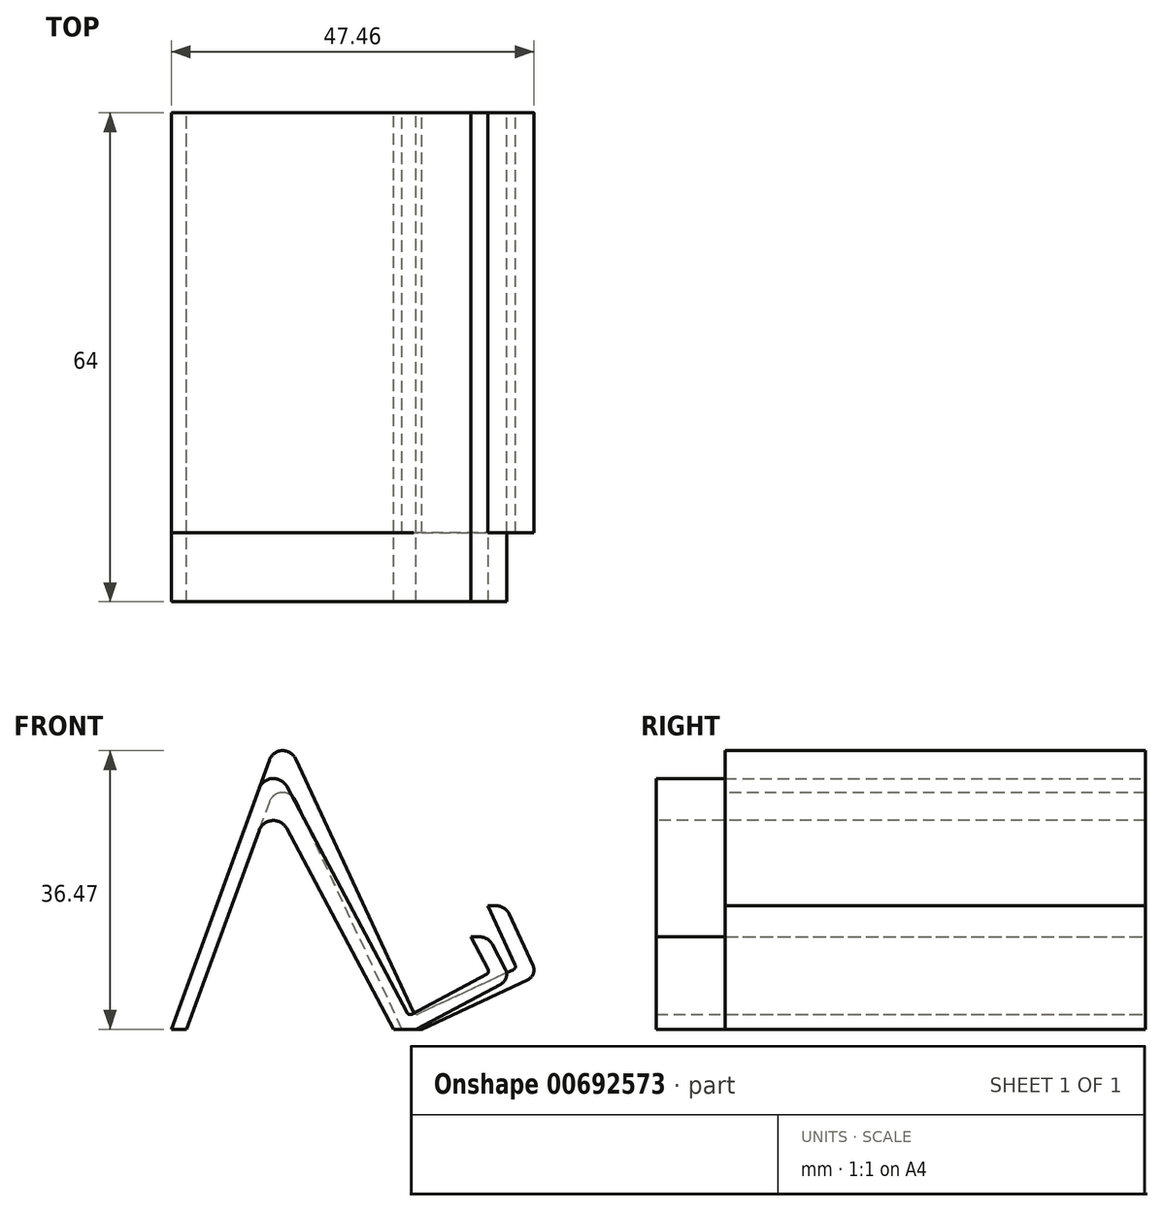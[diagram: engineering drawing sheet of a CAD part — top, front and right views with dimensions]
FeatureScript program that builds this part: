
annotation { "Feature Type Name" : "Feature", "Feature Type Description" : "" }
export const myFeature = defineFeature(function(context is Context, id is Id, definition is map)
    precondition{}
    {
        {
            var Q0;
            Q0=qCreatedBy(makeId("Front.planeOp"),FACE);
            var sketch = newSketch(context, id + "F0", { "sketchPlane" : qUnion([Q0])});
            skLineSegment(sketch, "E0", {"start": v(16.06, 0) * mm, "end": v(0, 30.21) * mm});
            skLineSegment(sketch, "E1", {"start": v(0, 30.21) * mm, "end": v(-11, 0) * mm});
            skLineSegment(sketch, "E2", {"start": v(-11, 0) * mm, "end": v(-13, 0) * mm});
            skLineSegment(sketch, "E3", {"start": v(-13, 0) * mm, "end": v(0, 35.7) * mm});
            skLineSegment(sketch, "E4", {"start": v(0, 35.7) * mm, "end": v(18.05, 1.77) * mm});
            skLineSegment(sketch, "E5", {"start": v(18.99, 0) * mm, "end": v(16.06, 0) * mm});
            skLineSegment(sketch, "E6", {"start": v(18.99, 0) * mm, "end": v(31.38, 6.6) * mm});
            skLineSegment(sketch, "E7", {"start": v(28.64, 7.4) * mm, "end": v(18.05, 1.77) * mm});
            skLineSegment(sketch, "E8", {"start": v(31.38, 6.6) * mm, "end": v(28.46, 12.08) * mm});
            skLineSegment(sketch, "E9", {"start": v(28.64, 7.4) * mm, "end": v(26.15, 12.08) * mm});
            skLineSegment(sketch, "E10", {"start": v(26.15, 12.08) * mm, "end": v(28.46, 12.08) * mm});
            skSolve(sketch);
        }
        {
            var Q0;
            Q0=makeQuery(id+"F0.imprint","IMPRINT",FACE,{"disambiguationData":[TD([[makeQuery(id+"F0.imprint","IMPRINT",EDGE,{"derivedFrom":sQuery(id+"F0.wireOp",EDGE,"E0")}),-1.0]])]});
            extrude(context, id + "F1", {"entities" : qUnion([Q0]), "depth" : 64 * mm, "offsetDistance" : 25 * mm});
        }
        {
            var Q0;
            Q0=makeQuery(id+"F1.opExtrude","SWEPT_EDGE",EDGE,{"disambiguationData":[OSD([sQuery(id+"F0.wireOp",EDGE,"E0"),sQuery(id+"F0.wireOp",EDGE,"E1")])]});
            var Q1;
            Q1=makeQuery(id+"F1.opExtrude","SWEPT_EDGE",EDGE,{"disambiguationData":[OSD([sQuery(id+"F0.wireOp",EDGE,"E3"),sQuery(id+"F0.wireOp",EDGE,"E4")])]});
            fillet(context, id + "F2", {"entities" : qUnion([Q0, Q1]), "radius" : 1.99 * mm, "tangentPropagation" : true, "allowEdgeOverflow" : false});
        }
        {
            var Q0;
            Q0=makeQuery(id+"F1.opExtrude","SWEPT_EDGE",EDGE,{"disambiguationData":[OSD([sQuery(id+"F0.wireOp",EDGE,"E4"),sQuery(id+"F0.wireOp",EDGE,"E7")])]});
            var Q1;
            Q1=makeQuery(id+"F1.opExtrude","SWEPT_EDGE",EDGE,{"disambiguationData":[OSD([sQuery(id+"F0.wireOp",EDGE,"E7"),sQuery(id+"F0.wireOp",EDGE,"E9")])]});
            fillet(context, id + "F3", {"entities" : qUnion([Q0, Q1]), "radius" : 0.42 * mm, "tangentPropagation" : true, "allowEdgeOverflow" : false});
        }
        {
            var Q0;
            Q0=makeQuery(id+"F1.opExtrude","SWEPT_EDGE",EDGE,{"disambiguationData":[OSD([sQuery(id+"F0.wireOp",EDGE,"E8"),sQuery(id+"F0.wireOp",EDGE,"E10")])]});
            fillet(context, id + "F4", {"entities" : qUnion([Q0]), "radius" : 1.8 * mm, "tangentPropagation" : true, "allowEdgeOverflow" : false});
        }
        {
            var Q0;
            Q0=makeQuery(id+"F1.opExtrude","SWEPT_EDGE",EDGE,{"disambiguationData":[OSD([sQuery(id+"F0.wireOp",EDGE,"E6"),sQuery(id+"F0.wireOp",EDGE,"E8")])]});
            fillet(context, id + "F5", {"entities" : qUnion([Q0]), "radius" : 1.45 * mm, "tangentPropagation" : true, "allowEdgeOverflow" : false});
        }
        {
            var Q0;
            Q0=qCreatedBy(makeId("Front.planeOp"),FACE);
            var sketch = newSketch(context, id + "F6", { "sketchPlane" : qUnion([Q0])});
            skLineSegment(sketch, "E11", {"start": v(17.18, 0) * mm, "end": v(1.34, 33.97) * mm});
            skLineSegment(sketch, "E12", {"start": v(1.34, 33.97) * mm, "end": v(-11.02, 0) * mm});
            skLineSegment(sketch, "E13", {"start": v(-11.02, 0) * mm, "end": v(-13.02, 0) * mm});
            skLineSegment(sketch, "E14", {"start": v(-13.02, 0) * mm, "end": v(1.34, 39.47) * mm});
            skLineSegment(sketch, "E15", {"start": v(1.34, 39.47) * mm, "end": v(18.9, 1.81) * mm});
            skLineSegment(sketch, "E16", {"start": v(19.75, 0) * mm, "end": v(17.18, 0) * mm});
            skLineSegment(sketch, "E17", {"start": v(19.75, 0) * mm, "end": v(34.92, 7.08) * mm});
            skLineSegment(sketch, "E18", {"start": v(32.18, 8) * mm, "end": v(18.9, 1.81) * mm});
            skLineSegment(sketch, "E19", {"start": v(34.92, 7.08) * mm, "end": v(30.68, 16.16) * mm});
            skLineSegment(sketch, "E20", {"start": v(32.18, 8) * mm, "end": v(28.38, 16.16) * mm});
            skLineSegment(sketch, "E21", {"start": v(28.38, 16.16) * mm, "end": v(30.68, 16.16) * mm});
            skSolve(sketch);
        }
        {
            var Q0;
            Q0=makeQuery(id+"F6.imprint","IMPRINT",FACE,{"disambiguationData":[TD([[makeQuery(id+"F6.imprint","IMPRINT",EDGE,{"derivedFrom":sQuery(id+"F6.wireOp",EDGE,"E11")}),-1.0]])]});
            extrude(context, id + "F7", {"entities" : qUnion([Q0]), "depth" : 55 * mm, "offsetDistance" : 25 * mm});
        }
        {
            var Q0;
            Q0=makeQuery(id+"F7.opExtrude","SWEPT_EDGE",EDGE,{"disambiguationData":[OSD([sQuery(id+"F6.wireOp",EDGE,"E14"),sQuery(id+"F6.wireOp",EDGE,"E15")])]});
            var Q1;
            Q1=makeQuery(id+"F7.opExtrude","SWEPT_EDGE",EDGE,{"disambiguationData":[OSD([sQuery(id+"F6.wireOp",EDGE,"E11"),sQuery(id+"F6.wireOp",EDGE,"E12")])]});
            fillet(context, id + "F8", {"entities" : qUnion([Q0, Q1]), "radius" : 1.86 * mm, "tangentPropagation" : true, "allowEdgeOverflow" : false});
        }
        {
            var Q0;
            Q0=makeQuery(id+"F7.opExtrude","SWEPT_EDGE",EDGE,{"disambiguationData":[OSD([sQuery(id+"F6.wireOp",EDGE,"E15"),sQuery(id+"F6.wireOp",EDGE,"E18")])]});
            var Q1;
            Q1=makeQuery(id+"F7.opExtrude","SWEPT_EDGE",EDGE,{"disambiguationData":[OSD([sQuery(id+"F6.wireOp",EDGE,"E18"),sQuery(id+"F6.wireOp",EDGE,"E20")])]});
            fillet(context, id + "F9", {"entities" : qUnion([Q0, Q1]), "radius" : 0.46 * mm, "tangentPropagation" : true, "allowEdgeOverflow" : false});
        }
        {
            var Q0;
            Q0=makeQuery(id+"F7.opExtrude","SWEPT_EDGE",EDGE,{"disambiguationData":[OSD([sQuery(id+"F6.wireOp",EDGE,"E19"),sQuery(id+"F6.wireOp",EDGE,"E21")])]});
            fillet(context, id + "F10", {"entities" : qUnion([Q0]), "radius" : 1.88 * mm, "tangentPropagation" : true, "allowEdgeOverflow" : false});
        }
        {
            var Q0;
            Q0=makeQuery(id+"F7.opExtrude","SWEPT_EDGE",EDGE,{"disambiguationData":[OSD([sQuery(id+"F6.wireOp",EDGE,"E17"),sQuery(id+"F6.wireOp",EDGE,"E19")])]});
            fillet(context, id + "F11", {"entities" : qUnion([Q0]), "radius" : 1.45 * mm, "tangentPropagation" : true, "allowEdgeOverflow" : false});
        }
    });
